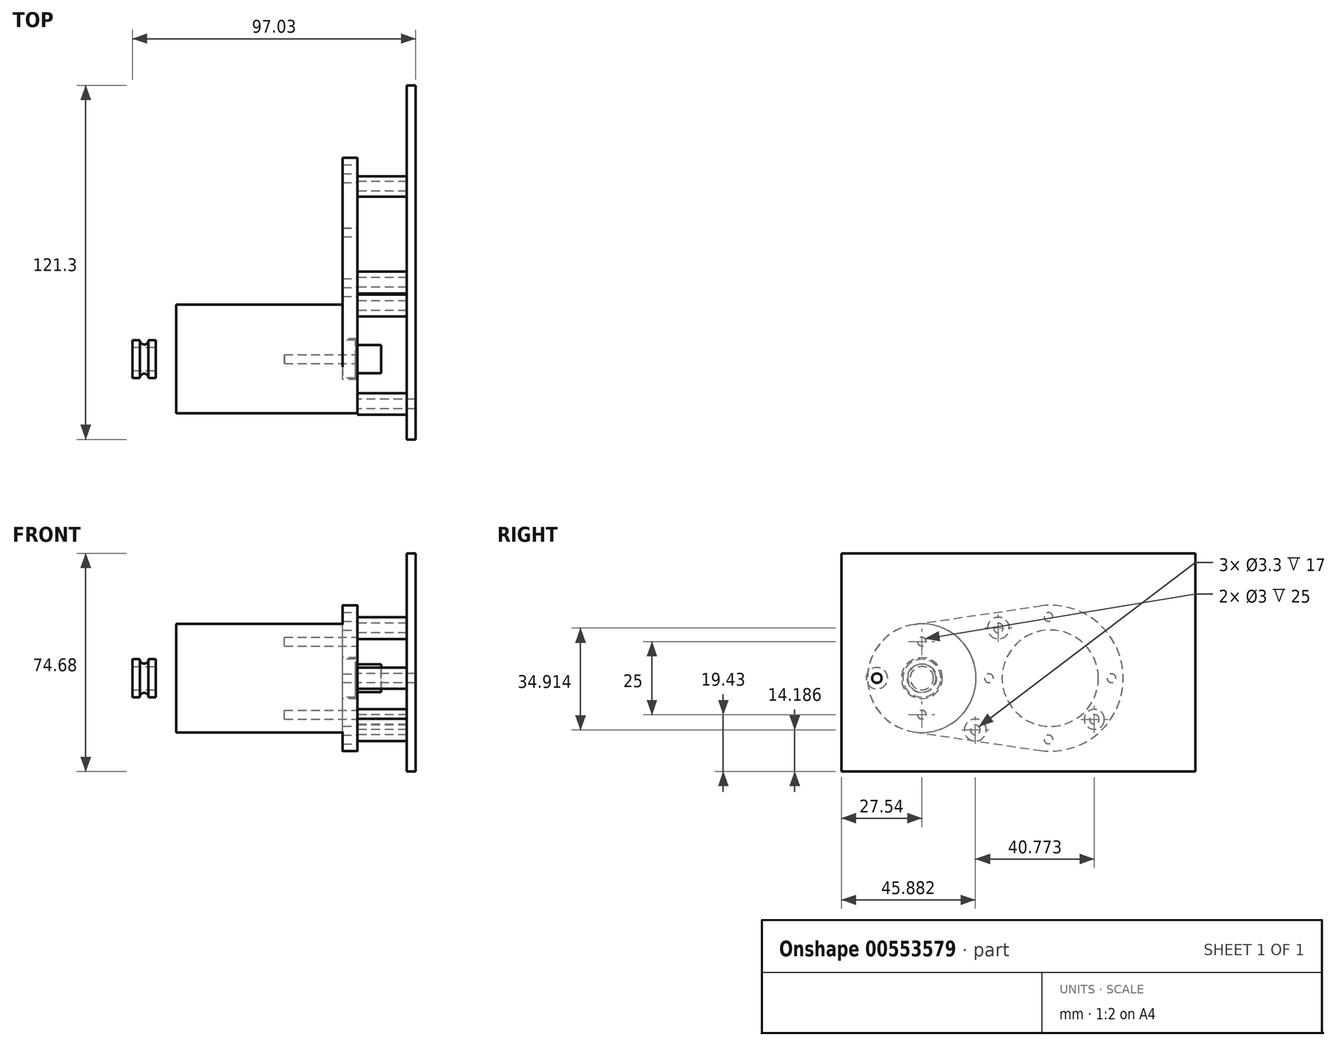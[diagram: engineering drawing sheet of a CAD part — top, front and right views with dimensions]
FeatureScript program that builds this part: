
annotation { "Feature Type Name" : "Feature", "Feature Type Description" : "" }
export const myFeature = defineFeature(function(context is Context, id is Id, definition is map)
    precondition{}
    {
        {
            var Q0;
            Q0=qCreatedBy(makeId("Right.planeOp"),FACE);
            var sketch = newSketch(context, id + "F0", { "sketchPlane" : qUnion([Q0])});
            skCircle(sketch, "E0", {"center": v(0, 0) * mm, "radius": 18.6 * mm});
            skSolve(sketch);
        }
        {
            var Q0;
            Q0=makeQuery(id+"F0.imprint","IMPRINT",FACE,{"disambiguationData":[TD([[makeQuery(id+"F0.imprint","IMPRINT",EDGE,{"derivedFrom":sQuery(id+"F0.wireOp",EDGE,"E0")}),1.0]])]});
            extrude(context, id + "F1", {"entities" : qUnion([Q0]), "depth" : 57 * mm, "offsetDistance" : 25 * mm});
        }
        {
            var Q0;
            Q0=makeQuery(id+"F1.opExtrude","CAP_FACE",FACE,{"disambiguationData":[OSD([sQuery(id+"F0.wireOp",EDGE,"E0")])],"isStart":false});
            var sketch = newSketch(context, id + "F2", { "sketchPlane" : qUnion([Q0])});
            skCircle(sketch, "E1", {"center": v(0, 0) * mm, "radius": 6.5 * mm});
            skSolve(sketch);
        }
        {
            var Q0;
            Q0=makeQuery(id+"F2.imprint","IMPRINT",FACE,{"disambiguationData":[TD([[makeQuery(id+"F2.imprint","IMPRINT",EDGE,{"derivedFrom":sQuery(id+"F2.wireOp",EDGE,"E1")}),1.0]])]});
            extrude(context, id + "F3", {"entities" : qUnion([Q0]), "operationType" : NewBodyOperationType.ADD, "depth" : 4.4 * mm, "offsetDistance" : 25 * mm});
        }
        {
            var Q0;
            Q0=makeQuery(id+"F3.opExtrude","CAP_FACE",FACE,{"disambiguationData":[OSD([sQuery(id+"F2.wireOp",EDGE,"E1")])],"isStart":false});
            var sketch = newSketch(context, id + "F4", { "sketchPlane" : qUnion([Q0])});
            skCircle(sketch, "E2", {"center": v(0, 0) * mm, "radius": 4.8 * mm});
            skSolve(sketch);
        }
        {
            var Q0;
            Q0=makeQuery(id+"F4.imprint","IMPRINT",FACE,{"disambiguationData":[TD([[makeQuery(id+"F4.imprint","IMPRINT",EDGE,{"derivedFrom":sQuery(id+"F4.wireOp",EDGE,"E2")}),1.0]])]});
            extrude(context, id + "F5", {"entities" : qUnion([Q0]), "operationType" : NewBodyOperationType.ADD, "depth" : 8.8 * mm, "offsetDistance" : 25 * mm});
        }
        {
            var Q0;
            Q0=makeQuery(id+"F1.opExtrude","CAP_FACE",FACE,{"disambiguationData":[OSD([sQuery(id+"F0.wireOp",EDGE,"E0")])],"isStart":false});
            var sketch = newSketch(context, id + "F6", { "sketchPlane" : qUnion([Q0])});
            skCircle(sketch, "E3", {"center": v(0, 0) * mm, "radius": 7 * mm});
            skCircle(sketch, "E4", {"center": v(0, 0) * mm, "radius": 20 * mm});
            skSolve(sketch);
        }
        {
            var Q0;
            Q0=makeQuery(id+"F6.imprint","IMPRINT",FACE,{"disambiguationData":[TD([[makeQuery(id+"F6.imprint","IMPRINT",EDGE,{"derivedFrom":sQuery(id+"F6.wireOp",EDGE,"E3")}),-1.0]])]});
            extrude(context, id + "F7", {"entities" : qUnion([Q0]), "depth" : 5 * mm, "offsetDistance" : 25 * mm});
        }
        {
            var Q0;
            Q0=makeQuery(id+"F7.opExtrude","CAP_FACE",FACE,{"disambiguationData":[OSD([sQuery(id+"F0.wireOp",EDGE,"E0"),sQuery(id+"F6.wireOp",EDGE,"E3")])],"isStart":false});
            var sketch = newSketch(context, id + "F8", { "sketchPlane" : qUnion([Q0])});
            skCircle(sketch, "E5", {"center": v(45, 0) * mm, "radius": 25 * mm});
            skCircle(sketch, "E6", {"center": v(45, 0) * mm, "radius": 16.5 * mm});
            skSolve(sketch);
        }
        {
            var Q0;
            Q0=makeQuery(id+"F8.imprint","IMPRINT",FACE,{"disambiguationData":[TD([[makeQuery(id+"F8.imprint","IMPRINT",EDGE,{"derivedFrom":sQuery(id+"F8.wireOp",EDGE,"E5")}),1.0]])]});
            extrude(context, id + "F9", {"entities" : qUnion([Q0]), "oppositeDirection" : true, "depth" : 5 * mm, "offsetDistance" : 25 * mm});
        }
        {
            var Q0;
            Q0=makeQuery(id+"F9.opExtrude","SWEPT_BODY",BODY,{"disambiguationData":[OSD([sQuery(id+"F8.wireOp",EDGE,"E5"),sQuery(id+"F8.wireOp",EDGE,"E6")])]});
            deleteBodies(context, id + "F10", {"entities" : qUnion([Q0])});
        }
        {
            var Q0;
            Q0=makeQuery(id+"F7.opExtrude","CAP_FACE",FACE,{"disambiguationData":[OSD([sQuery(id+"F0.wireOp",EDGE,"E0"),sQuery(id+"F6.wireOp",EDGE,"E3")])],"isStart":false});
            var sketch = newSketch(context, id + "F11", { "sketchPlane" : qUnion([Q0])});
            skLineSegment(sketch, "E7", {"start": v(-2.7, 18.4) * mm, "end": v(40.36, 24.73) * mm});
            skLineSegment(sketch, "E8", {"start": v(-2.7, -18.4) * mm, "end": v(40.36, -24.73) * mm});
            skArc(sketch, "E9", {"start": v(40.36, 24.73) * mm, "mid": v(69, 0) * mm, "end": v(40.36, -24.73) * mm});
            skCircle(sketch, "E10", {"center": v(44, 0) * mm, "radius": 16.5 * mm});
            skArc(sketch, "E11", {"start": v(-2.7, 18.4) * mm, "mid": v(18.6, 0) * mm, "end": v(-2.7, -18.4) * mm});
            skSolve(sketch);
        }
        {
            var Q0;
            Q0=makeQuery(id+"F11.imprint","IMPRINT",FACE,{"disambiguationData":[TD([[makeQuery(id+"F11.imprint","IMPRINT",EDGE,{"derivedFrom":sQuery(id+"F11.wireOp",EDGE,"E7")}),-1.0]])]});
            extrude(context, id + "F12", {"entities" : qUnion([Q0]), "operationType" : NewBodyOperationType.ADD, "oppositeDirection" : true, "depth" : 5 * mm, "offsetDistance" : 25 * mm});
        }
        {
            var Q0;
            Q0=makeQuery(id+"F12.boolean.opBoolean","MERGE",FACE,{"derivedFrom":[makeQuery(id+"F7.opExtrude","CAP_FACE",FACE,{"disambiguationData":[OSD([sQuery(id+"F0.wireOp",EDGE,"E0"),sQuery(id+"F6.wireOp",EDGE,"E3")])],"isStart":false}),makeQuery(id+"F12.opExtrude","CAP_FACE",FACE,{"disambiguationData":[OSD([sQuery(id+"F11.wireOp",EDGE,"E7"),sQuery(id+"F11.wireOp",EDGE,"E8"),sQuery(id+"F11.wireOp",EDGE,"E9"),sQuery(id+"F11.wireOp",EDGE,"E10"),sQuery(id+"F11.wireOp",EDGE,"E11")])],"isStart":true})]});
            var sketch = newSketch(context, id + "F13", { "sketchPlane" : qUnion([Q0])});
            skCircle(sketch, "E12", {"center": v(0, 12.5) * mm, "radius": 1.5 * mm});
            skCircle(sketch, "E13", {"center": v(0, -12.5) * mm, "radius": 1.5 * mm});
            skSolve(sketch);
        }
        {
            var Q0;
            Q0=makeQuery(id+"F13.imprint","IMPRINT",FACE,{"disambiguationData":[TD([[makeQuery(id+"F13.imprint","IMPRINT",EDGE,{"derivedFrom":sQuery(id+"F13.wireOp",EDGE,"E12")}),1.0]])]});
            var Q1;
            Q1=makeQuery(id+"F13.imprint","IMPRINT",FACE,{"disambiguationData":[TD([[makeQuery(id+"F13.imprint","IMPRINT",EDGE,{"derivedFrom":sQuery(id+"F13.wireOp",EDGE,"E13")}),1.0]])]});
            extrude(context, id + "F14", {"entities" : qUnion([Q0, Q1]), "operationType" : NewBodyOperationType.REMOVE, "oppositeDirection" : true, "depth" : 25 * mm, "offsetDistance" : 25 * mm});
        }
        {
            var Q0;
            Q0=makeQuery(id+"F12.boolean.opBoolean","MERGE",FACE,{"derivedFrom":[makeQuery(id+"F7.opExtrude","CAP_FACE",FACE,{"disambiguationData":[OSD([sQuery(id+"F0.wireOp",EDGE,"E0"),sQuery(id+"F6.wireOp",EDGE,"E3")])],"isStart":false}),makeQuery(id+"F12.opExtrude","CAP_FACE",FACE,{"disambiguationData":[OSD([sQuery(id+"F11.wireOp",EDGE,"E7"),sQuery(id+"F11.wireOp",EDGE,"E8"),sQuery(id+"F11.wireOp",EDGE,"E9"),sQuery(id+"F11.wireOp",EDGE,"E10"),sQuery(id+"F11.wireOp",EDGE,"E11")])],"isStart":true})]});
            var sketch = newSketch(context, id + "F15", { "sketchPlane" : qUnion([Q0])});
            skCircle(sketch, "E14", {"center": v(44, 0) * mm, "radius": 21 * mm, "construction": true});
            skCircle(sketch, "E15", {"center": v(43.39, 21) * mm, "radius": 1.5 * mm});
            skCircle(sketch, "E16", {"center": v(65, 0) * mm, "radius": 1.5 * mm});
            skPoint(sketch, "E16.centerSnap0", {"position": v(69, 0) * mm});
            skCircle(sketch, "E17", {"center": v(43.43, -21) * mm, "radius": 1.5 * mm});
            skCircle(sketch, "E18", {"center": v(23, 0) * mm, "radius": 1.5 * mm});
            skSolve(sketch);
        }
        {
            var Q0;
            Q0=makeQuery(id+"F15.imprint","IMPRINT",FACE,{"disambiguationData":[TD([[makeQuery(id+"F15.imprint","IMPRINT",EDGE,{"derivedFrom":sQuery(id+"F15.wireOp",EDGE,"E18")}),1.0]])]});
            var Q1;
            Q1=makeQuery(id+"F15.imprint","IMPRINT",FACE,{"disambiguationData":[TD([[makeQuery(id+"F15.imprint","IMPRINT",EDGE,{"derivedFrom":sQuery(id+"F15.wireOp",EDGE,"E15")}),1.0]])]});
            var Q2;
            Q2=makeQuery(id+"F15.imprint","IMPRINT",FACE,{"disambiguationData":[TD([[makeQuery(id+"F15.imprint","IMPRINT",EDGE,{"derivedFrom":sQuery(id+"F15.wireOp",EDGE,"E16")}),1.0]])]});
            var Q3;
            Q3=makeQuery(id+"F15.imprint","IMPRINT",FACE,{"disambiguationData":[TD([[makeQuery(id+"F15.imprint","IMPRINT",EDGE,{"derivedFrom":sQuery(id+"F15.wireOp",EDGE,"E17")}),1.0]])]});
            extrude(context, id + "F16", {"entities" : qUnion([Q0, Q1, Q2, Q3]), "operationType" : NewBodyOperationType.REMOVE, "oppositeDirection" : true, "depth" : 25 * mm, "offsetDistance" : 25 * mm});
        }
        {
            var Q0;
            Q0=qCreatedBy(makeId("Front.planeOp"),FACE);
            var sketch = newSketch(context, id + "F17", { "sketchPlane" : qUnion([Q0])});
            skLineSegment(sketch, "E19", {"start": v(0, 0) * mm, "end": v(-20.34, 0) * mm});
            skLineSegment(sketch, "E20", {"start": v(-15.03, 4) * mm, "end": v(-15.03, 6.5) * mm});
            skLineSegment(sketch, "E21", {"start": v(-15.03, 6.5) * mm, "end": v(-12.53, 6.5) * mm});
            skLineSegment(sketch, "E22", {"start": v(-7.03, 4) * mm, "end": v(-7.03, 6.5) * mm});
            skLineSegment(sketch, "E23", {"start": v(-7.03, 6.5) * mm, "end": v(-9.53, 6.5) * mm});
            skLineSegment(sketch, "E24", {"start": v(-15.03, 4) * mm, "end": v(-7.03, 4) * mm});
            skArc(sketch, "E25", {"start": v(-12.53, 6.5) * mm, "mid": v(-11.03, 5) * mm, "end": v(-9.53, 6.5) * mm});
            skSolve(sketch);
        }
        {
            var Q0;
            Q0=makeQuery(id+"F17.imprint","IMPRINT",FACE,{"disambiguationData":[TD([[makeQuery(id+"F17.imprint","IMPRINT",EDGE,{"derivedFrom":sQuery(id+"F17.wireOp",EDGE,"E20")}),-1.0]])]});
            var Q1;
            Q1=sQuery(id+"F17.wireOp",EDGE,"E19");
            revolve(context, id + "F18", {"entities" : qUnion([Q0]), "axis" : qUnion([Q1]), "revolveType" : RevolveType.FULL});
        }
        {
            var Q0;
            Q0=makeQuery(id+"F12.boolean.opBoolean","MERGE",FACE,{"derivedFrom":[makeQuery(id+"F7.opExtrude","CAP_FACE",FACE,{"disambiguationData":[OSD([sQuery(id+"F0.wireOp",EDGE,"E0"),sQuery(id+"F6.wireOp",EDGE,"E3")])],"isStart":false}),makeQuery(id+"F12.opExtrude","CAP_FACE",FACE,{"disambiguationData":[OSD([sQuery(id+"F11.wireOp",EDGE,"E7"),sQuery(id+"F11.wireOp",EDGE,"E8"),sQuery(id+"F11.wireOp",EDGE,"E9"),sQuery(id+"F11.wireOp",EDGE,"E10"),sQuery(id+"F11.wireOp",EDGE,"E11")])],"isStart":true})]});
            var sketch = newSketch(context, id + "F19", { "sketchPlane" : qUnion([Q0])});
            skCircle(sketch, "E26", {"center": v(0, 0) * mm, "radius": 7 * mm});
            skCircle(sketch, "E27", {"center": v(44, 0) * mm, "radius": 37 * mm});
            skSolve(sketch);
        }
        {
            var Q0;
            {var subQ1=sQuery(id+"F19.wireOp",EDGE,"E26");Q0=makeQuery(id+"F19.imprint","IMPRINT",FACE,{"disambiguationData":[TD([[makeQuery(id+"F19.imprint","IMPRINT",EDGE,{"derivedFrom":subQ1}),-1.0]])]});}
            var sketch = newSketch(context, id + "F20", { "sketchPlane" : qUnion([Q0])});
            skCircle(sketch, "E28", {"center": v(-15.42, 0) * mm, "radius": 1.65 * mm});
            skCircle(sketch, "E29", {"center": v(26.23, 17.17) * mm, "radius": 1.65 * mm});
            skCircle(sketch, "E30", {"center": v(59.11, -14.1) * mm, "radius": 1.65 * mm});
            skCircle(sketch, "E31", {"center": v(18.34, -17.74) * mm, "radius": 1.65 * mm});
            skCircle(sketch, "E32", {"center": v(26.23, 17.17) * mm, "radius": 3.73 * mm});
            skCircle(sketch, "E33", {"center": v(59.11, -14.1) * mm, "radius": 3.44 * mm});
            skCircle(sketch, "E34", {"center": v(18.34, -17.74) * mm, "radius": 3.78 * mm});
            skCircle(sketch, "E35", {"center": v(-15.42, 0) * mm, "radius": 3.68 * mm});
            skSolve(sketch);
        }
        {
            var Q0;
            Q0 = qSketchRegion(id + "F20", true);
            extrude(context, id + "F21", {"entities" : qUnion([Q0]), "depth" : 20 * mm, "offsetDistance" : 25 * mm});
        }
        {
            var Q0;
            Q0=makeQuery(id+"F21.opExtrude","CAP_FACE",FACE,{"disambiguationData":[OSD([sQuery(id+"F20.wireOp",EDGE,"E28"),sQuery(id+"F20.wireOp",EDGE,"E35")])],"isStart":false});
            var sketch = newSketch(context, id + "F22", { "sketchPlane" : qUnion([Q0])});
            skLineSegment(sketch, "E36.bottom", {"start": v(-27.54, 42.75) * mm, "end": v(93.76, 42.75) * mm});
            skLineSegment(sketch, "E36.top", {"start": v(-27.54, -31.93) * mm, "end": v(93.76, -31.93) * mm});
            skLineSegment(sketch, "E36.left", {"start": v(-27.54, 42.75) * mm, "end": v(-27.54, -31.93) * mm});
            skLineSegment(sketch, "E36.right", {"start": v(93.76, 42.75) * mm, "end": v(93.76, -31.93) * mm});
            skSolve(sketch);
        }
        {
            var Q0;
            Q0=makeQuery(id+"F22.imprint","IMPRINT",FACE,{"disambiguationData":[TD([[makeQuery(id+"F22.imprint","IMPRINT",EDGE,{"derivedFrom":sQuery(id+"F22.wireOp",EDGE,"E36.bottom")}),-1.0]])]});
            extrude(context, id + "F23", {"entities" : qUnion([Q0]), "operationType" : NewBodyOperationType.ADD, "oppositeDirection" : true, "depth" : 3 * mm, "offsetDistance" : 25 * mm});
        }
    });
